# Revit family: IS_Conca_T3953_BIM_IT
name_source: partatom
category: Furniture
revit_build: Autodesk Revit 2017 (Build: 20160225_1515(x64)
units: mm (PartAtom-declared; Revit-internal decimal feet)

## family parameters
Always vertical = No
Cut with Voids When Loaded = No
OmniClass Number = 23.45.05.14.21.11
OmniClass Title = Bath/Shower Units
Room Calculation Point = No
Shared = No
Work Plane-Based = No

## types (6) — shared parameters
BIMobject category = Storage
BIMobject category code = sanitary-storage
BIMobject main category = Sanitary
BIMobject main category code = sanitary
Installation instructions = https://www.idealspec.co.uk
Maniglia = No
NominalDepth = 505 mm  [stored 1.65682 ft]
NominalHeight = 80 mm  [stored 0.262467 ft]
NominalWidth = 1600 mm  [stored 5.24934 ft]
PiattoDoccia = No
Product group = Bathroom_Furniture
Uniclass 2015 Code = Pr_40_30_78_03
Uniclass 2015 Name = Bathroom cabinets
zero-valued in all types: AltezzaNominale, CostoDiSostituzione, DimensioneScarico, LarghezzaNominale, LunghezzaNominale, Nominal depth, Nominal height, ProfonditaNominale, SeatMaterial, SpessoreDelMateriale, SpilloverLivello, Weight Net (Kg)

## per-type parameters (varying)
| type | Model |
| T3953Y1 - Conca CONSOLE 160X50  WHMT - T3953 - Y1_MattWhite | T3953Y1 |
| T3953Y2 - Conca CONSOLE 160X50  WHMT - T3953 - Y2_MattAntracite | T3953Y2 |
| T3953Y3 - Conca CONSOLE 160X50  WHMT - T3953 - Y3_MattSunset | T3953Y3 |
| T3953Y4 - Conca CONSOLE 160X50  WHMT - T3953 - Y4_SmokedOak | T3953Y4 |
| T3953Y5 - Conca CONSOLE 160X50  WHMT - T3953 - Y5_DarkWalnut | T3953Y5 |
| T3953Y6 - Conca CONSOLE 160X50  WHMT - T3953 - Y6_LightOak | T3953Y6 |

note: [stored X ft] marks values corroborated as IEEE doubles in the binary element streams (Revit-internal decimal feet)

## geometry (parser evidence)
native form markers: Sweep x4
no freeform markers — native parametric forms only
